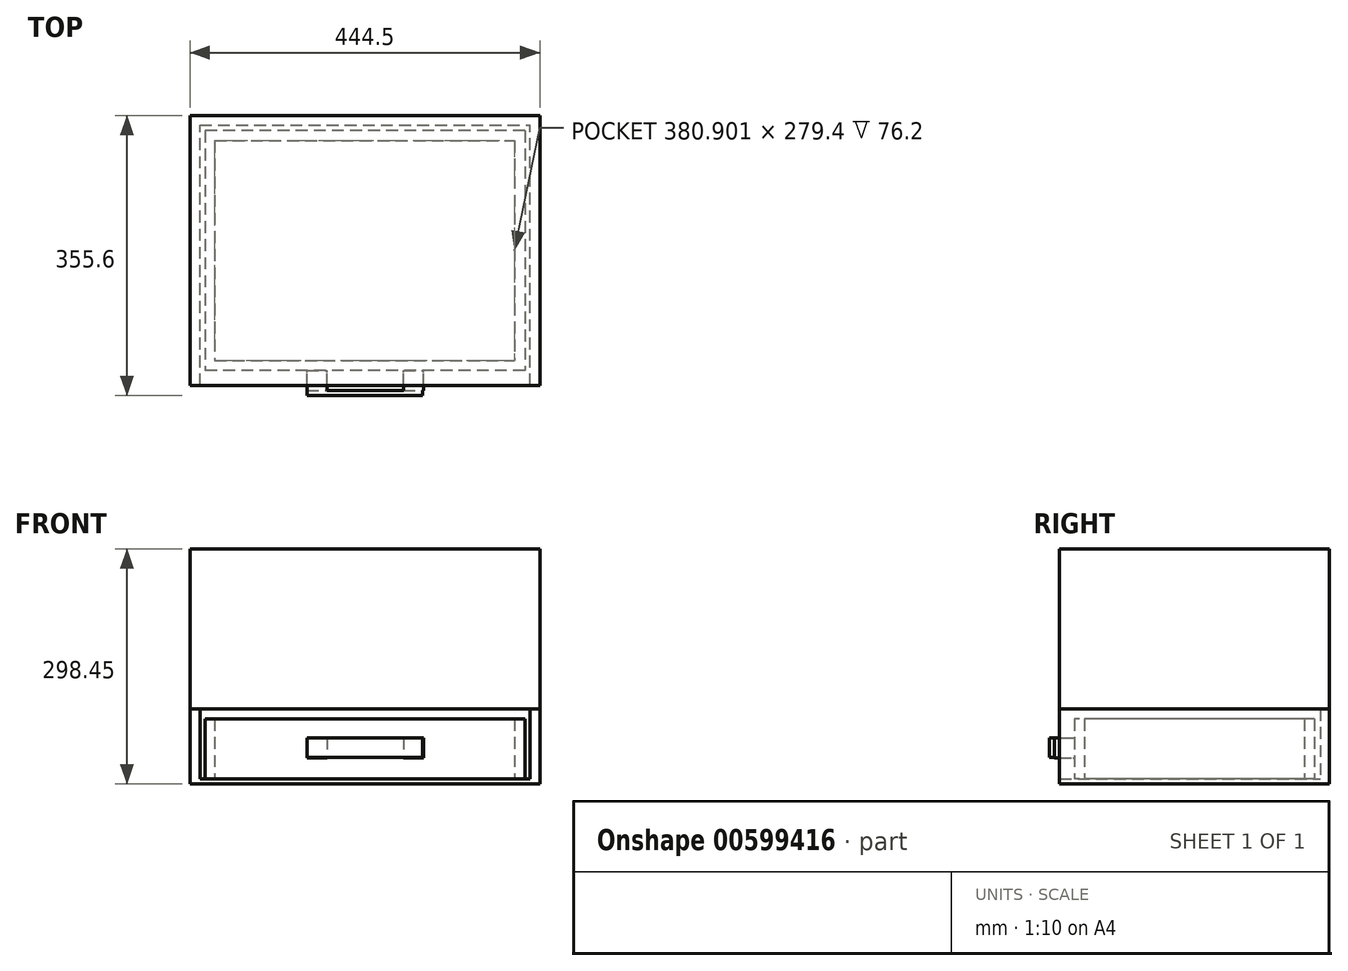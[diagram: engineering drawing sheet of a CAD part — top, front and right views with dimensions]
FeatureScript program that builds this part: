
annotation { "Feature Type Name" : "Feature", "Feature Type Description" : "" }
export const myFeature = defineFeature(function(context is Context, id is Id, definition is map)
    precondition{}
    {
        {
            var Q0;
            Q0=qCreatedBy(makeId("Top.planeOp"),FACE);
            var sketch = newSketch(context, id + "F0", { "sketchPlane" : qUnion([Q0])});
            skLineSegment(sketch, "E0.bottom", {"start": v(203.2, 152.4) * mm, "end": v(-203.2, 152.4) * mm});
            skLineSegment(sketch, "E0.top", {"start": v(203.2, -152.4) * mm, "end": v(-203.2, -152.4) * mm});
            skLineSegment(sketch, "E0.left", {"start": v(203.2, 152.4) * mm, "end": v(203.2, -152.4) * mm});
            skLineSegment(sketch, "E0.right", {"start": v(-203.2, 152.4) * mm, "end": v(-203.2, -152.4) * mm});
            skPoint(sketch, "E0.middle", {"position": v(0, 0) * mm});
            skSolve(sketch);
        }
        {
            var Q0;
            Q0=makeQuery(id+"F0.imprint","IMPRINT",FACE,{"disambiguationData":[TD([[makeQuery(id+"F0.imprint","IMPRINT",EDGE,{"derivedFrom":sQuery(id+"F0.wireOp",EDGE,"E0.bottom")}),1.0]])]});
            extrude(context, id + "F1", {"entities" : qUnion([Q0]), "depth" : 1 / 101.6 * mm, "offsetDistance" : 25.4 * mm});
        }
        {
            var Q0;
            Q0=makeQuery(id+"F1.opExtrude","CAP_FACE",FACE,{"disambiguationData":[OSD([sQuery(id+"F0.wireOp",EDGE,"E0.bottom"),sQuery(id+"F0.wireOp",EDGE,"E0.top"),sQuery(id+"F0.wireOp",EDGE,"E0.left"),sQuery(id+"F0.wireOp",EDGE,"E0.right")])],"isStart":false});
            var sketch = newSketch(context, id + "F2", { "sketchPlane" : qUnion([Q0])});
            skLineSegment(sketch, "E1.bottom", {"start": v(-203.2, -152.4) * mm, "end": v(203.2, -152.4) * mm});
            skLineSegment(sketch, "E1.top", {"start": v(-203.2, -139.7) * mm, "end": v(203.2, -139.7) * mm});
            skLineSegment(sketch, "E1.left", {"start": v(-203.2, -152.4) * mm, "end": v(-203.2, -139.7) * mm});
            skLineSegment(sketch, "E1.right", {"start": v(203.2, -152.4) * mm, "end": v(203.2, -139.7) * mm});
            skLineSegment(sketch, "E2.bottom", {"start": v(-203.2, 152.4) * mm, "end": v(203.2, 152.4) * mm});
            skLineSegment(sketch, "E2.top", {"start": v(-203.2, 139.7) * mm, "end": v(203.2, 139.7) * mm});
            skLineSegment(sketch, "E2.left", {"start": v(-203.2, 152.4) * mm, "end": v(-203.2, 139.7) * mm});
            skLineSegment(sketch, "E2.right", {"start": v(203.2, 152.4) * mm, "end": v(203.2, 139.7) * mm});
            skLineSegment(sketch, "E3.bottom", {"start": v(-203.2, 139.7) * mm, "end": v(-190.7, 139.7) * mm});
            skLineSegment(sketch, "E3.top", {"start": v(-203.2, -139.7) * mm, "end": v(-190.7, -139.7) * mm});
            skLineSegment(sketch, "E3.left", {"start": v(-203.2, 139.7) * mm, "end": v(-203.2, -139.7) * mm});
            skLineSegment(sketch, "E3.right", {"start": v(-190.7, 139.7) * mm, "end": v(-190.7, -139.7) * mm});
            skLineSegment(sketch, "E4.bottom", {"start": v(203.2, 139.7) * mm, "end": v(190.2, 139.7) * mm});
            skLineSegment(sketch, "E4.top", {"start": v(203.2, -139.7) * mm, "end": v(190.2, -139.7) * mm});
            skLineSegment(sketch, "E4.left", {"start": v(203.2, 139.7) * mm, "end": v(203.2, -139.7) * mm});
            skLineSegment(sketch, "E4.right", {"start": v(190.2, 139.7) * mm, "end": v(190.2, -139.7) * mm});
            skSolve(sketch);
        }
        {
            var Q0;
            Q0 = qSketchRegion(id + "F2", true);
            extrude(context, id + "F3", {"entities" : qUnion([Q0]), "operationType" : NewBodyOperationType.ADD, "depth" : 76.2 * mm, "offsetDistance" : 25.4 * mm});
        }
        {
            var Q0;
            Q0=makeQuery(id+"F1.opExtrude","CAP_FACE",FACE,{"disambiguationData":[OSD([sQuery(id+"F0.wireOp",EDGE,"E0.bottom"),sQuery(id+"F0.wireOp",EDGE,"E0.top"),sQuery(id+"F0.wireOp",EDGE,"E0.left"),sQuery(id+"F0.wireOp",EDGE,"E0.right")])],"isStart":true});
            var sketch = newSketch(context, id + "F4", { "sketchPlane" : qUnion([Q0])});
            skLineSegment(sketch, "E5.bottom", {"start": v(-222.25, 171.45) * mm, "end": v(222.25, 171.45) * mm});
            skLineSegment(sketch, "E5.top", {"start": v(-222.25, -171.45) * mm, "end": v(222.25, -171.45) * mm});
            skLineSegment(sketch, "E5.left", {"start": v(-222.25, 171.45) * mm, "end": v(-222.25, -171.45) * mm});
            skLineSegment(sketch, "E5.right", {"start": v(222.25, 171.45) * mm, "end": v(222.25, -171.45) * mm});
            skPoint(sketch, "E5.middle", {"position": v(0, 0) * mm});
            skSolve(sketch);
        }
        {
            var Q0;
            Q0 = qSketchRegion(id + "F4", true);
            extrude(context, id + "F5", {"entities" : qUnion([Q0]), "depth" : 6.35 * mm, "offsetDistance" : 25.4 * mm});
        }
        {
            var Q0;
            Q0=makeQuery(id+"F5.opExtrude","CAP_FACE",FACE,{"disambiguationData":[OSD([sQuery(id+"F4.wireOp",EDGE,"E5.bottom"),sQuery(id+"F4.wireOp",EDGE,"E5.top"),sQuery(id+"F4.wireOp",EDGE,"E5.left"),sQuery(id+"F4.wireOp",EDGE,"E5.right")])],"isStart":true});
            var sketch = newSketch(context, id + "F6", { "sketchPlane" : qUnion([Q0])});
            skLineSegment(sketch, "E6.bottom", {"start": v(222.25, -171.45) * mm, "end": v(209.55, -171.45) * mm});
            skLineSegment(sketch, "E6.top", {"start": v(222.25, 171.45) * mm, "end": v(209.55, 171.45) * mm});
            skLineSegment(sketch, "E6.left", {"start": v(222.25, -171.45) * mm, "end": v(222.25, 171.45) * mm});
            skLineSegment(sketch, "E6.right", {"start": v(209.55, -171.45) * mm, "end": v(209.55, 171.45) * mm});
            skLineSegment(sketch, "E7.left", {"start": v(209.55, -171.45) * mm, "end": v(209.55, -158.75) * mm});
            skLineSegment(sketch, "E8.bottom", {"start": v(-222.25, -171.45) * mm, "end": v(-209.55, -171.45) * mm});
            skLineSegment(sketch, "E8.top", {"start": v(-222.25, 171.45) * mm, "end": v(-209.55, 171.45) * mm});
            skLineSegment(sketch, "E8.left", {"start": v(-222.25, -171.45) * mm, "end": v(-222.25, 171.45) * mm});
            skLineSegment(sketch, "E8.right", {"start": v(-209.55, -171.45) * mm, "end": v(-209.55, 171.45) * mm});
            skLineSegment(sketch, "E9.left", {"start": v(-209.55, 171.45) * mm, "end": v(-209.55, 159.55) * mm});
            skLineSegment(sketch, "E9.right", {"start": v(209.55, 171.45) * mm, "end": v(209.55, 159.55) * mm});
            skLineSegment(sketch, "E10.bottom", {"start": v(-209.55, 171.45) * mm, "end": v(209.55, 171.45) * mm});
            skLineSegment(sketch, "E10.top", {"start": v(-209.55, 159.55) * mm, "end": v(209.55, 159.55) * mm});
            skSolve(sketch);
        }
        {
            var Q0;
            Q0 = qSketchRegion(id + "F6", true);
            extrude(context, id + "F7", {"entities" : qUnion([Q0]), "operationType" : NewBodyOperationType.ADD, "depth" : 88.9 * mm, "offsetDistance" : 25.4 * mm});
        }
        {
            var Q0;
            Q0=makeQuery(id+"F7.opExtrude","CAP_FACE",FACE,{"disambiguationData":[OSD([sQuery(id+"F6.wireOp",EDGE,"E6.bottom"),sQuery(id+"F6.wireOp",EDGE,"E6.top"),sQuery(id+"F6.wireOp",EDGE,"E6.left"),sQuery(id+"F6.wireOp",EDGE,"E6.right"),sQuery(id+"F6.wireOp",EDGE,"E7.left"),sQuery(id+"F6.wireOp",EDGE,"E8.bottom"),sQuery(id+"F6.wireOp",EDGE,"E8.top"),sQuery(id+"F6.wireOp",EDGE,"E8.left"),sQuery(id+"F6.wireOp",EDGE,"E8.right"),sQuery(id+"F6.wireOp",EDGE,"E10.bottom"),sQuery(id+"F6.wireOp",EDGE,"E10.top")])],"isStart":false});
            var sketch = newSketch(context, id + "F8", { "sketchPlane" : qUnion([Q0])});
            skLineSegment(sketch, "E11.bottom", {"start": v(-222.25, 171.45) * mm, "end": v(222.25, 171.45) * mm});
            skLineSegment(sketch, "E11.top", {"start": v(-222.25, -171.45) * mm, "end": v(222.25, -171.45) * mm});
            skLineSegment(sketch, "E11.left", {"start": v(-222.25, 171.45) * mm, "end": v(-222.25, -171.45) * mm});
            skLineSegment(sketch, "E11.right", {"start": v(222.25, 171.45) * mm, "end": v(222.25, -171.45) * mm});
            skSolve(sketch);
        }
        {
            var Q0;
            Q0 = qSketchRegion(id + "F8", true);
            extrude(context, id + "F9", {"entities" : qUnion([Q0]), "depth" : 203.2 * mm, "offsetDistance" : 25.4 * mm});
        }
        {
            var Q0;
            Q0=makeQuery(id+"F3.boolean.opBoolean","MERGE",FACE,{"derivedFrom":[makeQuery(id+"F1.opExtrude","SWEPT_FACE",FACE,{"disambiguationData":[OSD([sQuery(id+"F0.wireOp",EDGE,"E0.top")])]}),makeQuery(id+"F3.opExtrude","SWEPT_FACE",FACE,{"disambiguationData":[OSD([sQuery(id+"F2.wireOp",EDGE,"E1.bottom")])]})]});
            var sketch = newSketch(context, id + "F10", { "sketchPlane" : qUnion([Q0])});
            skLineSegment(sketch, "E12.bottom", {"start": v(-73.6, 52.22) * mm, "end": v(-48.2, 52.22) * mm});
            skLineSegment(sketch, "E12.top", {"start": v(-73.6, 26.82) * mm, "end": v(-48.2, 26.82) * mm});
            skLineSegment(sketch, "E12.left", {"start": v(-73.6, 52.22) * mm, "end": v(-73.6, 26.82) * mm});
            skLineSegment(sketch, "E12.right", {"start": v(-48.2, 52.22) * mm, "end": v(-48.2, 26.82) * mm});
            skLineSegment(sketch, "E13.bottom", {"start": v(49.04, 52.22) * mm, "end": v(74.44, 52.22) * mm});
            skLineSegment(sketch, "E13.top", {"start": v(49.04, 26.82) * mm, "end": v(74.44, 26.82) * mm});
            skLineSegment(sketch, "E13.left", {"start": v(49.04, 52.22) * mm, "end": v(49.04, 26.82) * mm});
            skLineSegment(sketch, "E13.right", {"start": v(74.44, 52.22) * mm, "end": v(74.44, 26.82) * mm});
            skSolve(sketch);
        }
        {
            var Q0;
            Q0 = qSketchRegion(id + "F10", true);
            extrude(context, id + "F11", {"entities" : qUnion([Q0]), "operationType" : NewBodyOperationType.ADD, "depth" : 25.4 * mm, "offsetDistance" : 25.4 * mm});
        }
        {
            var Q0;
            Q0=makeQuery(id+"F11.opExtrude","CAP_FACE",FACE,{"disambiguationData":[OSD([sQuery(id+"F10.wireOp",EDGE,"E12.bottom"),sQuery(id+"F10.wireOp",EDGE,"E12.top"),sQuery(id+"F10.wireOp",EDGE,"E12.left"),sQuery(id+"F10.wireOp",EDGE,"E12.right")])],"isStart":false});
            var sketch = newSketch(context, id + "F12", { "sketchPlane" : qUnion([Q0])});
            skLineSegment(sketch, "E14.bottom", {"start": v(-73.6, 52.22) * mm, "end": v(73.37, 52.22) * mm});
            skLineSegment(sketch, "E14.top", {"start": v(-73.6, 27.16) * mm, "end": v(73.37, 27.16) * mm});
            skLineSegment(sketch, "E14.left", {"start": v(-73.6, 52.22) * mm, "end": v(-73.6, 27.16) * mm});
            skLineSegment(sketch, "E14.right", {"start": v(73.37, 52.22) * mm, "end": v(73.37, 27.16) * mm});
            skSolve(sketch);
        }
        {
            var Q0;
            Q0 = qSketchRegion(id + "F12", true);
            extrude(context, id + "F13", {"entities" : qUnion([Q0]), "operationType" : NewBodyOperationType.ADD, "depth" : 6.35 * mm, "offsetDistance" : 25.4 * mm});
        }
    });
